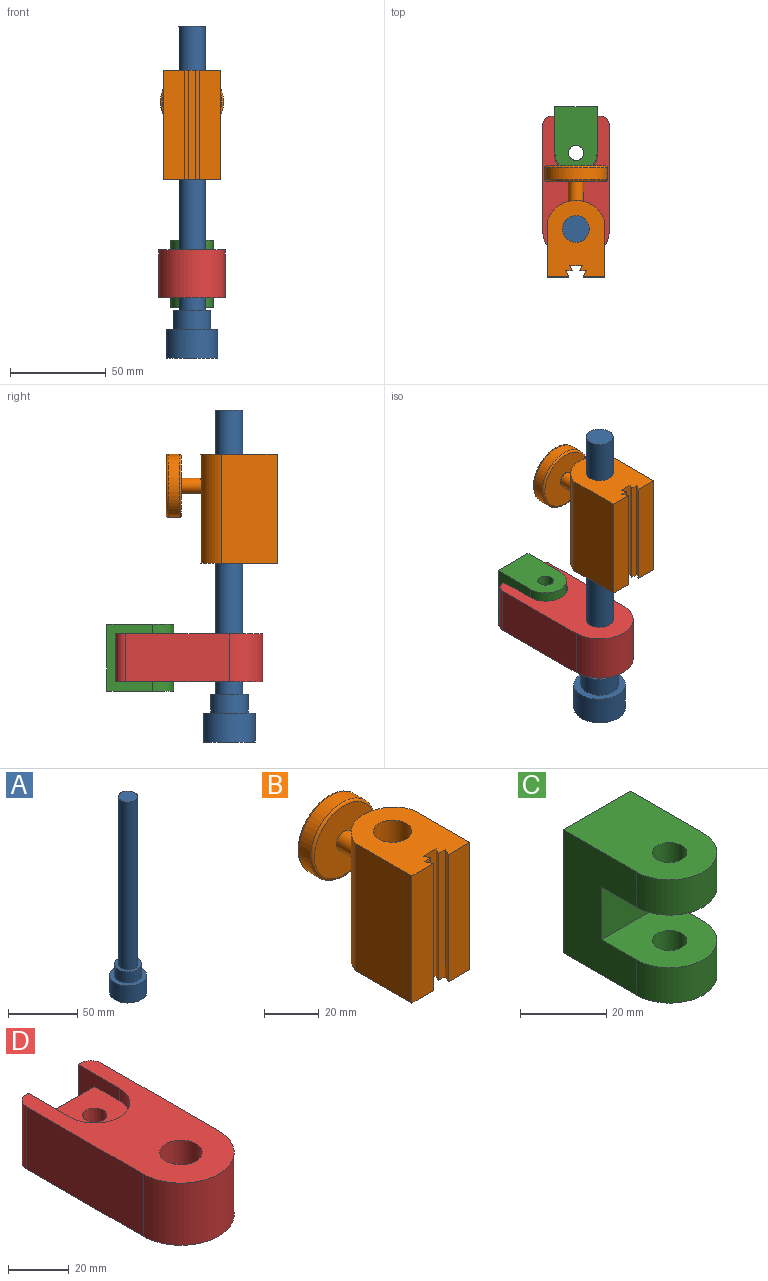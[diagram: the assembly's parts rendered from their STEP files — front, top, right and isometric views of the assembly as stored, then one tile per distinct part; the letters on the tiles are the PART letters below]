
ASSEMBLY  parts=4 mates=4
PART A: 7 faces, bbox 27x27x173.6 mm
  f0: cylinder r=9.81mm len=19.63mm, axis (0,0,1), area 610.5mm2, adj f3,f5
  f1: cylinder r=7mm len=148.6mm, axis (0,0,-1), area 6535.8mm2, adj f2,f3
  f2: plane 14x14mm, normal (0,0,1), area 153.9mm2, adj f1
  f3: plane 19.63x19.63mm, normal (0,0,1), area 148.7mm2, adj f0,f1
  f4: cylinder r=13.51mm len=27.02mm, axis (0,0,1), area 1281.7mm2, adj f5,f6
  f5: plane 27.02x27.02mm, normal (0,0,1), area 270.7mm2, adj f0,f4
  f6: plane 27.02x27.02mm, normal (0,0,-1), area 573.3mm2, adj f4
PART B: 21 faces, bbox 35.7x58x58.4 mm
  f0: cylinder r=15.74mm len=57mm, axis (0,0,-1), area 2214.5mm2, adj f3,f4,f13,f14,f15
  f1: plane 57x3.2mm, normal (-0.89,0.46,0), area 205.5mm2, adj f2,f12,f13,f14
  f2: plane 57x11.17mm, normal (0,-1,0), area 636.5mm2, adj f1,f3,f13,f14
  f3: plane 57x29.04mm, normal (1,0,0), area 1655.3mm2, adj f0,f2,f13,f14
  f4: plane 57x29.04mm, normal (-1,0,0), area 1655.3mm2, adj f0,f5,f13,f14
  f5: plane 57x11.17mm, normal (0,-1,0), area 636.5mm2, adj f4,f6,f13,f14
  f6: plane 57x3.2mm, normal (0.89,0.46,0), area 205.5mm2, adj f5,f7,f13,f14
  f7: plane 57x3.54mm, normal (0,-1,0), area 201.7mm2, adj f6,f8,f13,f14
  f8: plane 57x2.64mm, normal (0.89,0.46,0), area 169.7mm2, adj f7,f9,f13,f14
  f9: plane 57x6.65mm, normal (0,-1,0), area 378.8mm2, adj f8,f10,f13,f14
  f10: plane 57x2.64mm, normal (-0.89,0.46,0), area 169.7mm2, adj f9,f12,f13,f14
  f11: cylinder r=7mm len=57mm, axis (0,0,-1), area 2507mm2, adj f13,f14
  f12: plane 57x3.54mm, normal (0,-1,0), area 201.7mm2, adj f1,f10,f13,f14
  f13: plane 40x30mm, normal (0,0,1), area 914.5mm2, adj f0,f1,f2,f3,f4,f5,f6,f7
  f14: plane 40x30mm, normal (0,0,-1), area 914.5mm2, adj f0,f1,f2,f3,f4,f5,f6,f7
  f15: cylinder r=4mm len=10.52mm, axis (0,1,0), area 257.8mm2, adj f0,f18
  f16: cylinder r=16.5mm len=33mm, axis (0,-1,0), area 622mm2, adj f19,f20
  f17: plane 31x31mm, normal (0,1,0), area 754.8mm2, adj f20
  f18: plane 31x31mm, normal (0,-1,0), area 704.5mm2, adj f15,f19
  f19: torus R=15.5mm, axis (0,-1,0), area 159.3mm2, adj f16,f18
  f20: torus R=15.5mm, axis (0,-1,0), area 159.3mm2, adj f16,f17
PART C: 12 faces, bbox 22x35x35 mm
  f0: plane 35x24mm, normal (-1,0,0), area 667.5mm2, adj f1,f4,f5,f7,f8,f9,f10,f11
  f1: cylinder r=11mm len=22mm, axis (0,0,-1), area 345.6mm2, adj f0,f2,f8,f10
  f2: plane 35x24mm, normal (1,0,0), area 667.5mm2, adj f1,f4,f5,f7,f8,f9,f10,f11
  f3: cylinder r=4mm len=10mm, axis (0,0,-1), area 251.3mm2, adj f8,f10
  f4: plane 35x22mm, normal (0,1,0), area 770mm2, adj f0,f2,f7,f8
  f5: cylinder r=11mm len=22mm, axis (0,0,-1), area 345.6mm2, adj f0,f2,f7,f11
  f6: cylinder r=4mm len=10mm, axis (0,0,-1), area 251.3mm2, adj f7,f11
  f7: plane 35x22mm, normal (0,0,1), area 667.8mm2, adj f0,f2,f4,f5,f6
  f8: plane 35x22mm, normal (0,0,-1), area 667.8mm2, adj f0,f1,f2,f3,f4
  f9: plane 22x15mm, normal (0,-1,0), area 330mm2, adj f0,f2,f10,f11
  f10: plane 22.5x22mm, normal (0,0,1), area 392.8mm2, adj f0,f1,f2,f3,f9
  f11: plane 22.5x22mm, normal (0,0,-1), area 392.8mm2, adj f0,f2,f5,f6,f9
PART D: 18 faces, bbox 35x76.7x25 mm
  f0: plane 25x0.99mm, normal (0,1,0), area 24.7mm2, adj f1,f2,f10,f16
  f1: plane 76.74x34.98mm, normal (0,0,1), area 1737.5mm2, adj f0,f3,f4,f5,f6,f7,f9,f10
  f2: plane 76.74x34.98mm, normal (0,0,-1), area 1737.5mm2, adj f0,f3,f4,f5,f6,f7,f8,f9
  f3: cylinder r=17.49mm len=34.98mm, axis (0,0,-1), area 1373.5mm2, adj f1,f2,f4,f6
  f4: plane 54.25x25mm, normal (1,0,0), area 1356.2mm2, adj f1,f2,f3,f16
  f5: plane 25x0.99mm, normal (0,1,0), area 24.7mm2, adj f1,f2,f9,f17
  f6: plane 54.25x25mm, normal (-1,0,0), area 1356.2mm2, adj f1,f2,f3,f17
  f7: cylinder r=7mm len=25mm, axis (0,0,-1), area 1099.6mm2, adj f1,f2
  f8: cylinder r=11.5mm len=23mm, axis (0,0,-1), area 180.6mm2, adj f2,f9,f10,f13
  f9: plane 25x19.25mm, normal (1,0,0), area 308.7mm2, adj f1,f2,f5,f8,f11,f12,f13,f14
  f10: plane 25x19.25mm, normal (-1,0,0), area 308.7mm2, adj f0,f1,f2,f8,f11,f12,f13,f14
  f11: cylinder r=11.5mm len=23mm, axis (0,0,-1), area 180.6mm2, adj f1,f9,f10,f14
  f12: plane 23x15mm, normal (0,1,0), area 345mm2, adj f9,f10,f13,f14
  f13: plane 23x23mm, normal (0,0,-1), area 422mm2, adj f8,f9,f10,f12,f15
  f14: plane 23x23mm, normal (0,0,1), area 422mm2, adj f9,f10,f11,f12,f15
  f15: cylinder r=4mm len=15mm, axis (0,0,1), area 377mm2, adj f13,f14
  f16: cylinder r=5mm len=25mm, axis (0,0,-1), area 196.3mm2, adj f0,f1,f2,f4
  f17: cylinder r=5mm len=25mm, axis (0,0,1), area 196.3mm2, adj f1,f2,f5,f6
PLACE A t=(-23.42,-43.79,11.26)mm
PLACE B t=(-23.42,-43.79,33.96)mm
PLACE C t=(-23.42,-3.79,-44.04)mm
PLACE D t=(-23.42,-43.79,-44.04)mm
MATE cylindrical C.f3 <-> D.f8  axis (0,0,-1) through (-23.42,-3.79,-31.54)mm
MATE planar D.f14 <-> C.f11  axis (0,0,1) through (-34.92,-3.79,-36.54)mm
MATE slider D.f7 <-> A.f1  axis (0,0,-1) through (-23.42,-43.79,-44.04)mm
MATE slider B.f11 <-> A.f1  axis (0,0,-1) through (-23.42,-43.79,62.46)mm
